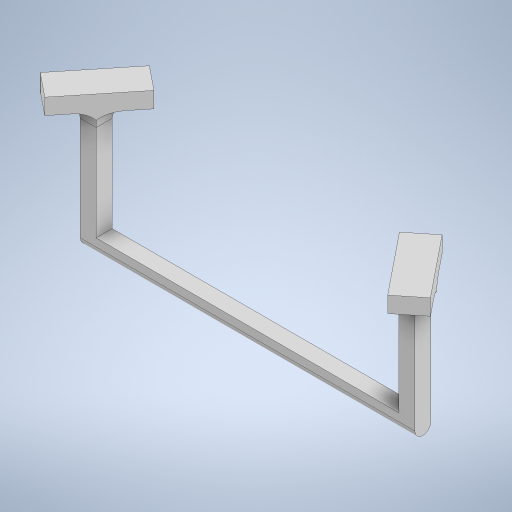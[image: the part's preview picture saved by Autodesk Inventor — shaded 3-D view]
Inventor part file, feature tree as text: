
AUTODESK INVENTOR PART (.ipt)
format: ipt  version: 2023 (Build 270158000, 158)  size: 521,216 bytes
history: native  units: in
note: dims shown in document units (in); Inventor stores cm internally (conversion verified against a paired STEP export)
features: extrude x6, sketch x6, fillet x2
ambient origin geometry x8: Origin, YZ Plane, XZ Plane, XY Plane, X Axis, Y Axis, Z Axis, Center Point
bodies: Solid1 (feature_tree)
feature tree (14):
  extrude  "Extrusion1"  Depth=0.25in
  fillet  "Fillet1"  Radius=1.75in
  extrude  "Extrusion2"  Depth=5.25in
  extrude  "Extrusion3"  Depth=0.125in
  extrude  "Extrusion4"  Depth=0.25in TaperAngle=0.0deg
  extrude  "Extrusion5"  Depth=0.0625in TaperAngle=0.0deg
  extrude  "Extrusion6"  Depth=0.25in
  fillet  "Fillet4"  [1 undecoded]
  sketch  "Sketch1"  dims[d1=2.0in d2=0.25in d3=1.75in]
  sketch  "Sketch2"  dims[d4=4.75in d5=5.25in]
  sketch  "Sketch6"  dims[d6=0.25in d7=0.0in d8=0.125in]
  sketch  "Sketch7"  dims[d11=0.25in d12=0.0in d32=0.0625in d33=0.0in]
  sketch  "Sketch8"  dims[d34=0.0625in d35=0.0in d36=0.0625in d37=0.0in]
  sketch  "Sketch9"  dims[d38=0.0625in d39=0.0in d50=0.25in d9=0.0in d10=0.0in d27=0.5in d28=0.0344in d29=0.5in d30=0.0344in d43=0.0in d44=0.0in d45=0.0in d46=0.0in]
note: 1 required parameter value undecoded (feature->parameter linkage not recoverable at this tier; creation-order binding heuristic only, values carry confidence <= 0.55)
